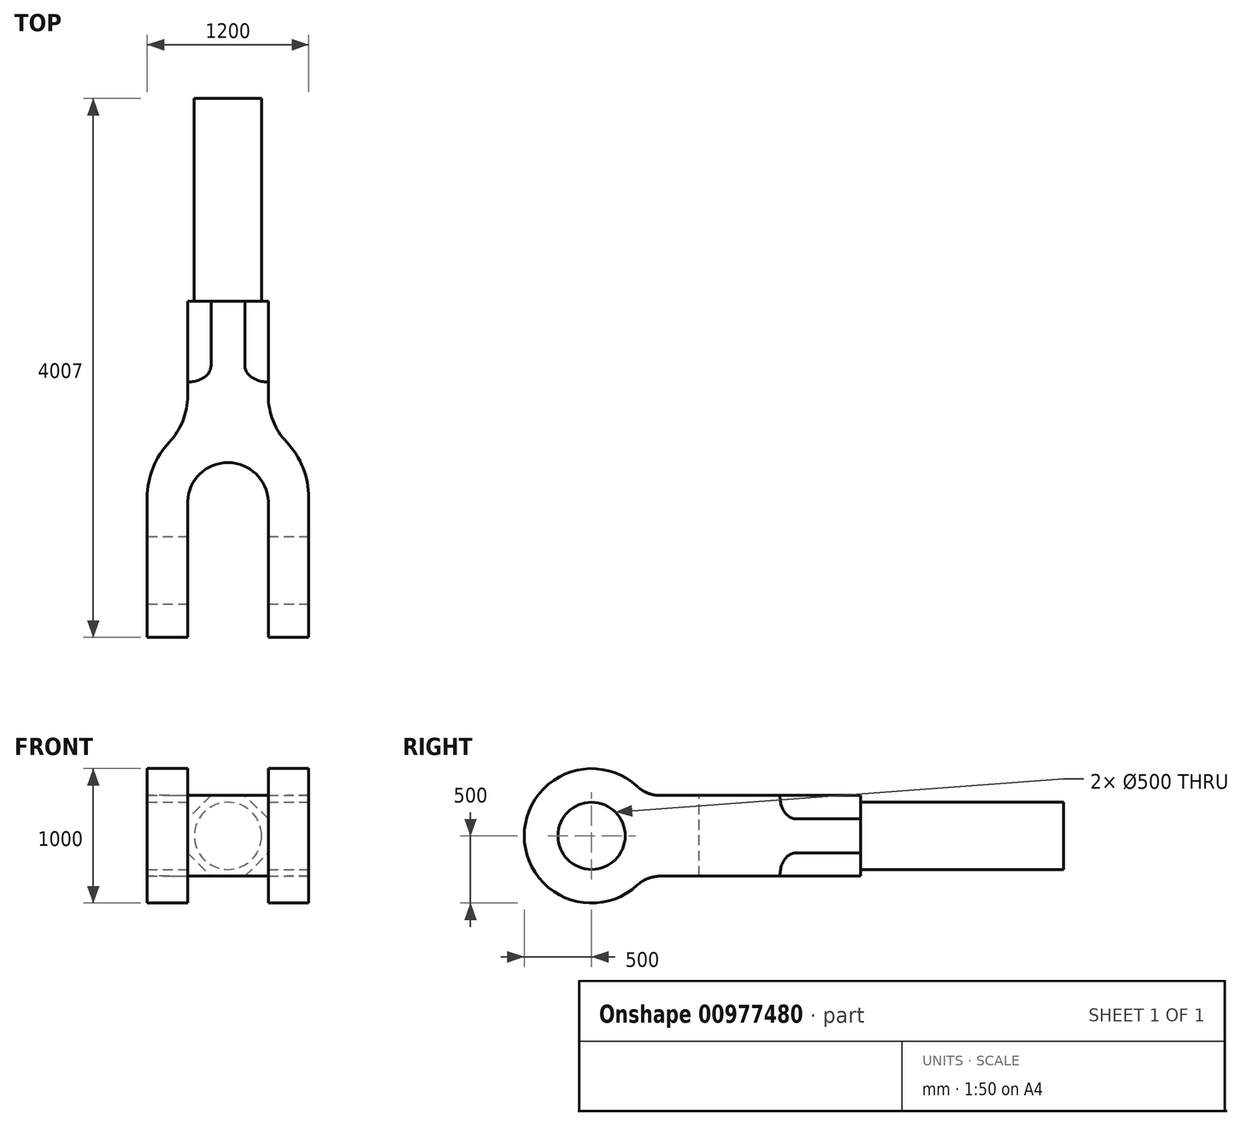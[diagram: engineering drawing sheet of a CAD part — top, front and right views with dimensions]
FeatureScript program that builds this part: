
annotation { "Feature Type Name" : "Feature", "Feature Type Description" : "" }
export const myFeature = defineFeature(function(context is Context, id is Id, definition is map)
    precondition{}
    {
        {
            var Q0;
            Q0=qCreatedBy(makeId("Top.planeOp"),FACE);
            var sketch = newSketch(context, id + "F0", { "sketchPlane" : qUnion([Q0])});
            skLineSegment(sketch, "E0.bottom", {"start": v(0, 0) * mm, "end": v(-1200, 0) * mm});
            skLineSegment(sketch, "E0.top", {"start": v(0, 2500) * mm, "end": v(-1200, 2500) * mm});
            skLineSegment(sketch, "E0.left", {"start": v(0, 0) * mm, "end": v(0, 2500) * mm});
            skLineSegment(sketch, "E0.right", {"start": v(-1200, 0) * mm, "end": v(-1200, 2500) * mm});
            skSolve(sketch);
        }
        {
            var Q0;
            Q0 = qSketchRegion(id + "F0", true);
            extrude(context, id + "F1", {"entities" : qUnion([Q0]), "depth" : 1000 * mm, "offsetDistance" : 25 * mm});
        }
        {
            var Q0;
            Q0=makeQuery(id+"F1.opExtrude","CAP_FACE",FACE,{"disambiguationData":[OSD([sQuery(id+"F0.wireOp",EDGE,"E0.bottom"),sQuery(id+"F0.wireOp",EDGE,"E0.top"),sQuery(id+"F0.wireOp",EDGE,"E0.left"),sQuery(id+"F0.wireOp",EDGE,"E0.right")])],"isStart":false});
            var sketch = newSketch(context, id + "F2", { "sketchPlane" : qUnion([Q0])});
            skLineSegment(sketch, "E1", {"start": v(-600, 2500) * mm, "end": v(-600, 0) * mm, "construction": true});
            skArc(sketch, "E2", {"start": v(-300, 1000) * mm, "mid": v(-600, 1300) * mm, "end": v(-900, 1000) * mm});
            skArc(sketch, "E3", {"start": v(-1036.36, 1451.8) * mm, "mid": v(-600, 440) * mm, "end": v(-163.64, 1451.8) * mm});
            skLineSegment(sketch, "E4", {"start": v(-900, 2500) * mm, "end": v(-900, 1794.98) * mm});
            skLineSegment(sketch, "E5.MirrorCS", {"start": v(-300, 2500) * mm, "end": v(-300, 1794.98) * mm});
            skLineSegment(sketch, "E6.5", {"start": v(0, 0) * mm, "end": v(0, 2500) * mm});
            skLineSegment(sketch, "E6.6", {"start": v(0, 2500) * mm, "end": v(-1200, 2500) * mm});
            skLineSegment(sketch, "E6.7", {"start": v(-1200, 0) * mm, "end": v(-1200, 2500) * mm});
            skLineSegment(sketch, "E6.8", {"start": v(0, 0) * mm, "end": v(-1200, 0) * mm});
            skPoint(sketch, "E7.visualSharp", {"position": v(-900, 1559.62) * mm});
            skArc(sketch, "E7.filletArc", {"start": v(-1036.36, 1451.8) * mm, "mid": v(-935.34, 1610.35) * mm, "end": v(-900, 1794.98) * mm});
            skPoint(sketch, "E8.visualSharp", {"position": v(-300, 1559.62) * mm});
            skArc(sketch, "E8.filletArc", {"start": v(-300, 1794.98) * mm, "mid": v(-264.66, 1610.35) * mm, "end": v(-163.64, 1451.8) * mm});
            skLineSegment(sketch, "E9", {"start": v(-300, 1000) * mm, "end": v(-300, 0) * mm});
            skLineSegment(sketch, "E10.MirrorCS", {"start": v(-900, 1000) * mm, "end": v(-900, 0) * mm});
            skSolve(sketch);
        }
        {
            var Q0;
            {var subQ0=sQuery(id+"F2.wireOp",EDGE,"E2");Q0=makeQuery(id+"F2.imprint","IMPRINT",FACE,{"disambiguationData":[TD([[makeQuery(id+"F2.imprint","IMPRINT",EDGE,{"derivedFrom":subQ0}),1.0]])]});}
            var Q1;
            {var subQ0=sQuery(id+"F2.wireOp",EDGE,"E10.MirrorCS");var subQ1=sQuery(id+"F2.wireOp",EDGE,"E3");var subQ2=makeQuery(id+"F2.imprint","INTERSECT",VERTEX,{"derivedFrom":[subQ1,subQ0]});Q1=makeQuery(id+"F2.imprint","IMPRINT",FACE,{"disambiguationData":[TD([[makeQuery(id+"F2.imprint","IMPRINT",EDGE,{"disambiguationData":[TD([[subQ2,-1.0]])],"derivedFrom":subQ1}),-1.0]])]});}
            var Q2;
            {var subQ5=sQuery(id+"F2.wireOp",EDGE,"E4");Q2=makeQuery(id+"F2.imprint","IMPRINT",FACE,{"disambiguationData":[TD([[makeQuery(id+"F2.imprint","IMPRINT",EDGE,{"derivedFrom":subQ5}),-1.0]])]});}
            var Q3;
            {var subQ5=sQuery(id+"F2.wireOp",EDGE,"E5.MirrorCS");Q3=makeQuery(id+"F2.imprint","IMPRINT",FACE,{"disambiguationData":[TD([[makeQuery(id+"F2.imprint","IMPRINT",EDGE,{"derivedFrom":subQ5}),1.0]])]});}
            extrude(context, id + "F3", {"entities" : qUnion([Q0, Q1, Q2, Q3]), "operationType" : NewBodyOperationType.REMOVE, "endBound" : BoundingType.THROUGH_ALL, "oppositeDirection" : true, "depth" : 25 * mm, "offsetDistance" : 25 * mm});
        }
        {
            var Q0;
            Q0=makeQuery(id+"F1.opExtrude","SWEPT_FACE",FACE,{"disambiguationData":[OSD([sQuery(id+"F0.wireOp",EDGE,"E0.left")])]});
            var sketch = newSketch(context, id + "F4", { "sketchPlane" : qUnion([Q0])});
            skPoint(sketch, "E11.centerSnap0", {"position": v(520, 1000) * mm});
            skPoint(sketch, "E11.centerSnap1", {"position": v(0, 500) * mm});
            skArc(sketch, "E12", {"start": v(839.93, 866.67) * mm, "mid": v(0, 500) * mm, "end": v(839.93, 133.33) * mm});
            skCircle(sketch, "E13", {"center": v(500, 500) * mm, "radius": 250 * mm});
            skLineSegment(sketch, "E14", {"start": v(500, 500) * mm, "end": v(2623.96, 500) * mm, "construction": true});
            skLineSegment(sketch, "E15.bottom", {"start": v(2500, 800) * mm, "end": v(1009.9, 800) * mm});
            skLineSegment(sketch, "E15.top", {"start": v(2500, 200) * mm, "end": v(1009.9, 200) * mm});
            skLineSegment(sketch, "E15.left", {"start": v(2500, 800) * mm, "end": v(2500, 200) * mm});
            skPoint(sketch, "E16.visualSharp", {"position": v(900, 800) * mm});
            skArc(sketch, "E16.filletArc", {"start": v(839.93, 866.67) * mm, "mid": v(918.61, 817.26) * mm, "end": v(1009.9, 800) * mm});
            skPoint(sketch, "E17.visualSharp", {"position": v(900, 200) * mm});
            skArc(sketch, "E17.filletArc", {"start": v(1009.9, 200) * mm, "mid": v(918.61, 182.74) * mm, "end": v(839.93, 133.33) * mm});
            skLineSegment(sketch, "E18.0", {"start": v(0, 1000) * mm, "end": v(1040, 1000) * mm});
            skLineSegment(sketch, "E18.1", {"start": v(0, 1000) * mm, "end": v(0, 0) * mm});
            skLineSegment(sketch, "E18.2", {"start": v(0, 0) * mm, "end": v(1040, 0) * mm});
            skLineSegment(sketch, "E18.3", {"start": v(1040, 0) * mm, "end": v(1451.8, 0) * mm});
            skLineSegment(sketch, "E18.4", {"start": v(1794.98, 0) * mm, "end": v(1451.8, 0) * mm});
            skLineSegment(sketch, "E18.5", {"start": v(2500, 0) * mm, "end": v(1794.98, 0) * mm});
            skLineSegment(sketch, "E18.6", {"start": v(2500, 0) * mm, "end": v(2500, 1000) * mm});
            skLineSegment(sketch, "E18.7", {"start": v(2500, 1000) * mm, "end": v(1794.98, 1000) * mm});
            skLineSegment(sketch, "E18.8", {"start": v(1794.98, 1000) * mm, "end": v(1451.8, 1000) * mm});
            skLineSegment(sketch, "E18.9", {"start": v(1040, 1000) * mm, "end": v(1451.8, 1000) * mm});
            skSolve(sketch);
        }
        {
            var Q0;
            {var subQ0=sQuery(id+"F4.wireOp",EDGE,"E18.0");var subQ1=sQuery(id+"F4.wireOp",EDGE,"E12");var subQ2=makeQuery(id+"F4.imprint","INTERSECT",VERTEX,{"derivedFrom":[subQ1,subQ0]});Q0=makeQuery(id+"F4.imprint","IMPRINT",FACE,{"disambiguationData":[TD([[makeQuery(id+"F4.imprint","IMPRINT",EDGE,{"disambiguationData":[TD([[subQ2,-1.0]])],"derivedFrom":subQ1}),-1.0]])]});}
            var Q1;
            {var subQ0=sQuery(id+"F4.wireOp",EDGE,"E18.1");var subQ1=sQuery(id+"F4.wireOp",EDGE,"E12");var subQ2=makeQuery(id+"F4.imprint","INTERSECT",VERTEX,{"derivedFrom":[subQ1,subQ0]});Q1=makeQuery(id+"F4.imprint","IMPRINT",FACE,{"disambiguationData":[TD([[makeQuery(id+"F4.imprint","IMPRINT",EDGE,{"disambiguationData":[TD([[subQ2,-1.0]])],"derivedFrom":subQ1}),-1.0]])]});}
            var Q2;
            {var subQ7=sQuery(id+"F4.wireOp",EDGE,"E17.filletArc");Q2=makeQuery(id+"F4.imprint","IMPRINT",FACE,{"disambiguationData":[TD([[makeQuery(id+"F4.imprint","IMPRINT",EDGE,{"derivedFrom":subQ7}),1.0]])]});}
            var Q3;
            {var subQ6=sQuery(id+"F4.wireOp",EDGE,"E18.3");Q3=makeQuery(id+"F4.imprint","IMPRINT",FACE,{"disambiguationData":[TD([[makeQuery(id+"F4.imprint","IMPRINT",EDGE,{"derivedFrom":subQ6}),1.0]])]});}
            var Q4;
            {var subQ5=sQuery(id+"F4.wireOp",EDGE,"E16.filletArc");Q4=makeQuery(id+"F4.imprint","IMPRINT",FACE,{"disambiguationData":[TD([[makeQuery(id+"F4.imprint","IMPRINT",EDGE,{"derivedFrom":subQ5}),1.0]])]});}
            var Q5;
            {var subQ0=sQuery(id+"F4.wireOp",EDGE,"E18.7");Q5=makeQuery(id+"F4.imprint","IMPRINT",FACE,{"disambiguationData":[TD([[makeQuery(id+"F4.imprint","IMPRINT",EDGE,{"derivedFrom":subQ0}),1.0]])]});}
            var Q6;
            Q6=makeQuery(id+"F4.imprint","IMPRINT",FACE,{"disambiguationData":[TD([[makeQuery(id+"F4.imprint","IMPRINT",EDGE,{"derivedFrom":sQuery(id+"F4.wireOp",EDGE,"E13")}),1.0]])]});
            extrude(context, id + "F5", {"entities" : qUnion([Q0, Q1, Q2, Q3, Q4, Q5, Q6]), "operationType" : NewBodyOperationType.REMOVE, "endBound" : BoundingType.THROUGH_ALL, "oppositeDirection" : true, "depth" : 25 * mm, "offsetDistance" : 25 * mm});
        }
        {
            var Q0;
            Q0=makeQuery(id+"F1.opExtrude","SWEPT_FACE",FACE,{"disambiguationData":[OSD([sQuery(id+"F0.wireOp",EDGE,"E0.top")])]});
            var sketch = newSketch(context, id + "F6", { "sketchPlane" : qUnion([Q0])});
            skLineSegment(sketch, "E19", {"start": v(300, 200) * mm, "end": v(900, 800) * mm, "construction": true});
            skCircle(sketch, "E20", {"center": v(600, 500) * mm, "radius": 250 * mm});
            skLineSegment(sketch, "E21", {"start": v(900, 800) * mm, "end": v(726, 800) * mm});
            skLineSegment(sketch, "E22", {"start": v(726, 800) * mm, "end": v(900, 626) * mm});
            skLineSegment(sketch, "E23", {"start": v(900, 626) * mm, "end": v(900, 800) * mm});
            skLineSegment(sketch, "E24.1.0", {"start": v(300, 800) * mm, "end": v(300, 626) * mm});
            skLineSegment(sketch, "E24.1.1", {"start": v(300, 626) * mm, "end": v(474, 800) * mm});
            skLineSegment(sketch, "E24.2.0", {"start": v(300, 200) * mm, "end": v(474, 200) * mm});
            skLineSegment(sketch, "E24.2.1", {"start": v(474, 200) * mm, "end": v(300, 374) * mm});
            skLineSegment(sketch, "E24.3.0", {"start": v(900, 200) * mm, "end": v(900, 374) * mm});
            skLineSegment(sketch, "E24.3.1", {"start": v(900, 374) * mm, "end": v(726, 200) * mm});
            skSolve(sketch);
        }
        {
            var Q0;
            Q0=makeQuery(id+"F6.imprint","IMPRINT",FACE,{"disambiguationData":[TD([[makeQuery(id+"F6.imprint","IMPRINT",EDGE,{"derivedFrom":sQuery(id+"F6.wireOp",EDGE,"E21")}),1.0]])]});
            var Q1;
            {var subQ0=sQuery(id+"F6.wireOp",EDGE,"E24.1.0");Q1=makeQuery(id+"F6.imprint","IMPRINT",FACE,{"disambiguationData":[TD([[makeQuery(id+"F6.imprint","IMPRINT",EDGE,{"derivedFrom":subQ0}),-1.0]])]});}
            var Q2;
            {var subQ0=sQuery(id+"F6.wireOp",EDGE,"E24.2.0");Q2=makeQuery(id+"F6.imprint","IMPRINT",FACE,{"disambiguationData":[TD([[makeQuery(id+"F6.imprint","IMPRINT",EDGE,{"derivedFrom":subQ0}),-1.0]])]});}
            var Q3;
            {var subQ0=sQuery(id+"F6.wireOp",EDGE,"E24.3.0");Q3=makeQuery(id+"F6.imprint","IMPRINT",FACE,{"disambiguationData":[TD([[makeQuery(id+"F6.imprint","IMPRINT",EDGE,{"derivedFrom":subQ0}),1.0]])]});}
            extrude(context, id + "F7", {"entities" : qUnion([Q0, Q1, Q2, Q3]), "operationType" : NewBodyOperationType.REMOVE, "oppositeDirection" : true, "depth" : 600 * mm, "offsetDistance" : 25 * mm});
        }
        {
            var Q0;
            Q0=makeQuery(id+"F1.opExtrude","SWEPT_FACE",FACE,{"disambiguationData":[OSD([sQuery(id+"F0.wireOp",EDGE,"E0.top")])]});
            var sketch = newSketch(context, id + "F8", { "sketchPlane" : qUnion([Q0])});
            skCircle(sketch, "E25", {"center": v(600, 500) * mm, "radius": 250 * mm});
            skPoint(sketch, "E25.centerSnap0", {"position": v(600, 800) * mm});
            skPoint(sketch, "E25.centerSnap1", {"position": v(900, 500) * mm});
            skSolve(sketch);
        }
        {
            var Q0;
            Q0 = qSketchRegion(id + "F8", true);
            extrude(context, id + "F9", {"entities" : qUnion([Q0]), "operationType" : NewBodyOperationType.ADD, "depth" : 1507 * mm, "offsetDistance" : 25 * mm});
        }
        {
            var Q0;
            Q0=makeQuery(id+"F7.boolean.opBoolean","COPY",EDGE,{"derivedFrom":makeQuery(id+"F7.opExtrude","CAP_EDGE",EDGE,{"disambiguationData":[OSD([sQuery(id+"F6.wireOp",EDGE,"E22")])],"isStart":false})});
            var Q1;
            Q1=makeQuery(id+"F7.boolean.opBoolean","COPY",EDGE,{"derivedFrom":makeQuery(id+"F7.opExtrude","CAP_EDGE",EDGE,{"disambiguationData":[OSD([sQuery(id+"F6.wireOp",EDGE,"E24.1.1")])],"isStart":false})});
            var Q2;
            Q2=makeQuery(id+"F7.boolean.opBoolean","COPY",EDGE,{"derivedFrom":makeQuery(id+"F7.opExtrude","CAP_EDGE",EDGE,{"disambiguationData":[OSD([sQuery(id+"F6.wireOp",EDGE,"E24.3.1")])],"isStart":false})});
            var Q3;
            Q3=makeQuery(id+"F7.boolean.opBoolean","COPY",EDGE,{"derivedFrom":makeQuery(id+"F7.opExtrude","CAP_EDGE",EDGE,{"disambiguationData":[OSD([sQuery(id+"F6.wireOp",EDGE,"E24.2.1")])],"isStart":false})});
            fillet(context, id + "F10", {"entities" : qUnion([Q0, Q1, Q2, Q3]), "radius" : 120 * mm, "tangentPropagation" : true, "allowEdgeOverflow" : false});
        }
    });
